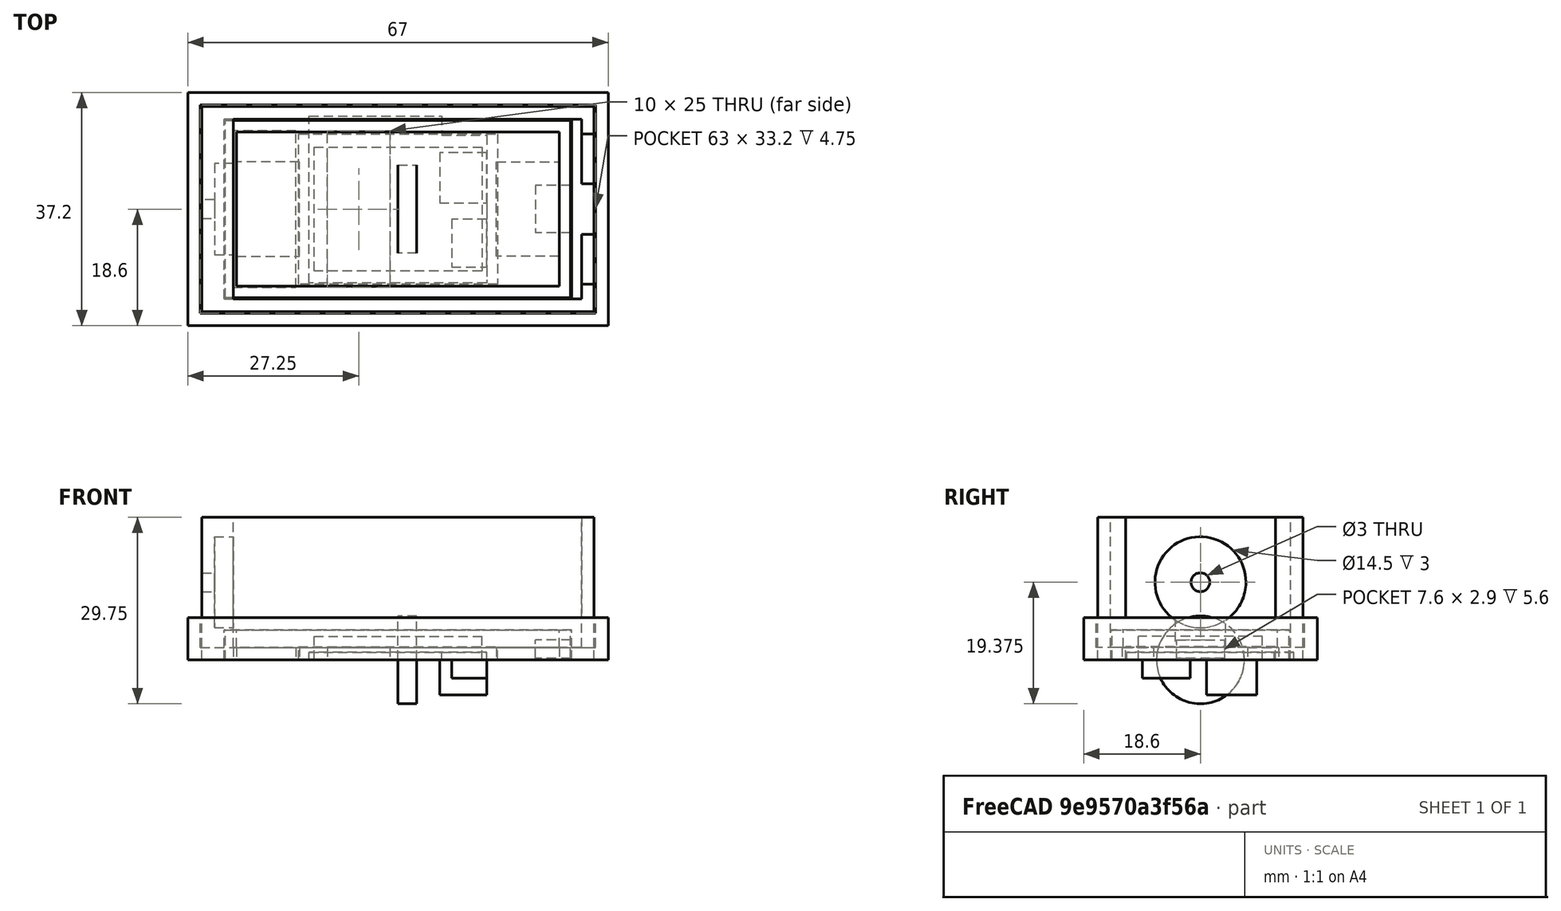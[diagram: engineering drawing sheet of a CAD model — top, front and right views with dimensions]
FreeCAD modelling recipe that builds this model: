
FCSTD DOCUMENT  (FreeCAD 0.20R29177 (Git))
Label: SniffingDetectorBox
License: All rights reserved
LicenseURL: http://en.wikipedia.org/wiki/All_rights_reserved
objects: Sketcher::SketchObject×20, PartDesign::Pad×13, PartDesign::Body×8, App::Part×8, PartDesign::Pocket×7, Mesh::Feature×2, Spreadsheet::Sheet×1
note: 68 computed .brp shape members not serialized (recipe doc carries the construction recipe); baked Part::Feature solids carry a one-line shape summary decoded from their .brp

FEATURE [Spreadsheet::Sheet] Spreadsheet  label="pars"
  cells = A1=ESPWidth; B1(ESPWidth)=28.2; A2=ESPLength; B2(ESPLength)=55; A3=USBWidth; B3(USBWidth)=7.6; A4=USBHeight; B4(USBHeight)=2.9; A5=USBLength; B5(USBLength)=5.6; A6=ESPHeight; B6(ESPHeight)=4.75; A7=ESPBoardHeight; B7(ESPBoardHeight)=1.6; A8=MicroDiam; B8(MicroDiam)=14; A9=MicroHeight; B9(MicroHeight)=3; A10=SDWidth; B10(SDWidth)=23.9; A11=SDLength; B11(SDLength)=31.7; A12=SDHeigth; B12(SDHeigth)=2.1; A13=ShieldWidthMax; B13(ShieldWidthMax)=26.6; A14=ShieldWidthMin; B14(ShieldWidthMin)=23.5; A15=ShieldLength; B15(ShieldLength)=28.3; A16=ShieldBoardHeight; B16(ShieldBoardHeight)=1.2; A17=ShieldPlugWidth; B17(ShieldPlugWidth)=8; A18=ShieldPlugHeight; B18(ShieldPlugHeight)=5.6; A19=ShieldPlugLength; B19(ShieldPlugLength)=7.5; A20=BatteryWidth; B20(BatteryWidth)=19.75; A21=BatteryLength; B21(BatteryLength)=26.75; A22=BatteryHeigth; B22(BatteryHeigth)=3.75; A23=Tolerance; B23(Tolerance)=0.5; A24=WallThick; B24(WallThick)=2
FEATURE [Sketcher::SketchObject] Sketch  label="BatterySketch"
  FullyConstrained = true
  MapMode = 5
  Support = -> [XY_Plane002]
  expr: Constraints[10] = <<pars>>.BatteryLength
  expr: Constraints[9] = <<pars>>.BatteryWidth
  sketch-geometry (4):
    g0: LineSegment StartX=-13.375 StartY=9.875 StartZ=0 EndX=13.375 EndY=9.875 EndZ=0
    g1: LineSegment StartX=13.375 StartY=9.875 StartZ=0 EndX=13.375 EndY=-9.875 EndZ=0
    g2: LineSegment StartX=13.375 StartY=-9.875 StartZ=0 EndX=-13.375 EndY=-9.875 EndZ=0
    g3: LineSegment StartX=-13.375 StartY=-9.875 StartZ=0 EndX=-13.375 EndY=9.875 EndZ=0
  constraints (11):
    c: Coincident(g0,g1)
    c: Coincident(g1,g2)
    c: Coincident(g2,g3)
    c: Coincident(g3,g0)
    c: Horizontal(g0)
    c: Horizontal(g2)
    c: Vertical(g1)
    c: Vertical(g3)
    c: Symmetric(g0,g1,g-1)
    c: DistanceY(g1,g1) = 19.75
    c: DistanceX(g0,g0) = 26.75
FEATURE [PartDesign::Pad] Pad
  Direction = (0,0,1)
  Length = 3.75
  Length2 = 10
  Profile = -> Sketch
  ReferenceAxis = -> Sketch [N_Axis]
  Type = 0
  expr: Length = <<pars>>.BatteryHeigth
FEATURE [PartDesign::Body] Body001  label="BatteryBody"
  Group = -> [Sketch,Pad]
  Origin = -> Origin002
  Tip = -> Pad
FEATURE [App::Part] Part001  label="Battery"
  Group = -> [Body001]
  Origin = -> Origin003
  Placement = pos=(-10,0,11.5) rot=(0,0,1;0rad)
FEATURE [Sketcher::SketchObject] Sketch001  label="SDCardSketch"
  FullyConstrained = true
  MapMode = 5
  Support = -> [XY_Plane005]
  expr: Constraints[10] = <<pars>>.SDLength
  expr: Constraints[9] = <<pars>>.SDWidth
  sketch-geometry (4):
    g0: LineSegment StartX=-15.85 StartY=11.95 StartZ=0 EndX=15.85 EndY=11.95 EndZ=0
    g1: LineSegment StartX=15.85 StartY=11.95 StartZ=0 EndX=15.85 EndY=-11.95 EndZ=0
    g2: LineSegment StartX=15.85 StartY=-11.95 StartZ=0 EndX=-15.85 EndY=-11.95 EndZ=0
    g3: LineSegment StartX=-15.85 StartY=-11.95 StartZ=0 EndX=-15.85 EndY=11.95 EndZ=0
  constraints (11):
    c: Coincident(g0,g1)
    c: Coincident(g1,g2)
    c: Coincident(g2,g3)
    c: Coincident(g3,g0)
    c: Horizontal(g0)
    c: Horizontal(g2)
    c: Vertical(g1)
    c: Vertical(g3)
    c: Symmetric(g0,g1,g-1)
    c: DistanceY(g1,g1) = 23.9
    c: DistanceX(g0,g0) = 31.7
FEATURE [PartDesign::Pad] Pad001
  Direction = (0,0,1)
  Length = 2.1
  Length2 = 10
  Profile = -> Sketch001
  ReferenceAxis = -> Sketch001 [N_Axis]
  Type = 0
  expr: Length = <<pars>>.SDHeigth
FEATURE [PartDesign::Body] Body002  label="SDCardBody"
  Group = -> [Sketch001,Pad001]
  Origin = -> Origin005
  Tip = -> Pad001
FEATURE [App::Part] Part002  label="SDCard"
  Group = -> [Body002]
  Origin = -> Origin004
  Placement = pos=(23,0,6.5) rot=(0,0,1;0rad)
FEATURE [Sketcher::SketchObject] Sketch002  label="MicroSketch"
  FullyConstrained = true
  MapMode = 5
  Placement = pos=(0,0,0) rot=(0.57735,0.57735,0.57735;2.0944rad)
  Support = -> [YZ_Plane007]
  expr: Constraints[1] = <<pars>>.MicroDiam
  sketch-geometry (1):
    g0: Circle CenterX=0 CenterY=0 CenterZ=0 NormalX=0 NormalY=0 NormalZ=1 AngleXU=0 Radius=7
  constraints (2):
    c: Coincident(g0,g-1)
    c: Diameter(g0) = 14
FEATURE [PartDesign::Pad] Pad002
  Direction = (1,-2e-16,3e-16)
  Length = 3
  Length2 = 10
  Placement = pos=(0,0,0) rot=(0.57735,0.57735,0.57735;2.0944rad)
  Profile = -> Sketch002
  ReferenceAxis = -> Sketch002 [N_Axis]
  Type = 0
  expr: Length = <<pars>>.MicroHeight
FEATURE [PartDesign::Body] Body003  label="MicroBody"
  Group = -> [Sketch002,Pad002]
  Origin = -> Origin007
  Tip = -> Pad002
FEATURE [App::Part] Part003  label="Micro"
  Group = -> [Body003]
  Origin = -> Origin006
  Placement = pos=(-29,0,12.5) rot=(0,0,1;0rad)
FEATURE [Sketcher::SketchObject] Sketch003  label="ESPSketch"
  FullyConstrained = true
  MapMode = 5
  Support = -> [XY_Plane009]
  expr: Constraints[10] = <<pars>>.ESPLength
  expr: Constraints[9] = <<pars>>.ESPWidth
  sketch-geometry (4):
    g0: LineSegment StartX=-27.5 StartY=14.1 StartZ=0 EndX=27.5 EndY=14.1 EndZ=0
    g1: LineSegment StartX=27.5 StartY=14.1 StartZ=0 EndX=27.5 EndY=-14.1 EndZ=0
    g2: LineSegment StartX=27.5 StartY=-14.1 StartZ=0 EndX=-27.5 EndY=-14.1 EndZ=0
    g3: LineSegment StartX=-27.5 StartY=-14.1 StartZ=0 EndX=-27.5 EndY=14.1 EndZ=0
  constraints (11):
    c: Coincident(g0,g1)
    c: Coincident(g1,g2)
    c: Coincident(g2,g3)
    c: Coincident(g3,g0)
    c: Horizontal(g0)
    c: Horizontal(g2)
    c: Vertical(g1)
    c: Vertical(g3)
    c: Symmetric(g0,g1,g-1)
    c: DistanceY(g1,g1) = 28.2
    c: DistanceX(g0,g0) = 55
FEATURE [PartDesign::Pad] Pad003
  Direction = (0,0,1)
  Length = 4.75
  Length2 = 10
  Profile = -> Sketch003
  ReferenceAxis = -> Sketch003 [N_Axis]
  Type = 0
  expr: Length = <<pars>>.ESPHeight
FEATURE [Sketcher::SketchObject] Sketch004
  ExternalGeometry = -> [Pad003]
  FullyConstrained = true
  MapMode = 5
  Placement = pos=(27.5,0,0) rot=(0.57735,0.57735,0.57735;2.0944rad)
  Support = -> [Pad003]
  expr: Constraints[10] = <<pars>>.ESPBoardHeight
  expr: Constraints[7] = Spreadsheet.USBHeight
  expr: Constraints[8] = Spreadsheet.USBWidth
  sketch-geometry (4):
    g0: LineSegment StartX=-3.8 StartY=3.15 StartZ=0 EndX=3.8 EndY=3.15 EndZ=0
    g1: LineSegment StartX=3.8 StartY=3.15 StartZ=0 EndX=3.8 EndY=0.25 EndZ=0
    g2: LineSegment StartX=3.8 StartY=0.25 StartZ=0 EndX=-3.8 EndY=0.25 EndZ=0
    g3: LineSegment StartX=-3.8 StartY=0.25 StartZ=0 EndX=-3.8 EndY=3.15 EndZ=0
  constraints (11):
    c: Coincident(g0,g1)
    c: Coincident(g1,g2)
    c: Coincident(g2,g3)
    c: Coincident(g3,g0)
    c: Horizontal(g0)
    c: Vertical(g1)
    c: Vertical(g3)
    c: DistanceY(g1,g1) = 2.9
    c: DistanceX(g0,g0) = 7.6
    c: Symmetric(g2,g1,g-2)
    c: DistanceY(g0,g-3) = 1.6
FEATURE [PartDesign::Pocket] Pocket
  BaseFeature = -> Pad003
  Direction = (-1,0,0)
  Length = 5.6
  Length2 = 5
  Profile = -> Sketch004
  ReferenceAxis = -> Sketch004 [N_Axis]
  Type = 0
  expr: Length = Spreadsheet.USBLength
FEATURE [PartDesign::Body] Body004  label="ESPBody"
  Group = -> [Sketch003,Pad003,Sketch004,Pocket]
  Origin = -> Origin009
  Tip = -> Pocket
FEATURE [App::Part] Part004  label="ESP"
  Group = -> [Body004]
  Origin = -> Origin008
  Placement = pos=(1.5,0,2) rot=(0,0,1;0rad)
FEATURE [Sketcher::SketchObject] Sketch005
  FullyConstrained = true
  MapMode = 5
  Support = -> [XY_Plane011]
  expr: Constraints[13] = <<pars>>.ShieldWidthMax - <<pars>>.ShieldWidthMin
  expr: Constraints[7] = <<pars>>.ShieldWidthMin
  expr: Constraints[8] = <<pars>>.ShieldLength
  sketch-geometry (6):
    g0: LineSegment StartX=7 StartY=11.75 StartZ=0 EndX=14.15 EndY=11.75 EndZ=0
    g1: LineSegment StartX=14.15 StartY=11.75 StartZ=0 EndX=14.15 EndY=-11.75 EndZ=0
    g2: LineSegment StartX=14.15 StartY=-11.75 StartZ=0 EndX=-14.15 EndY=-11.75 EndZ=0
    g3: LineSegment StartX=-14.15 StartY=-11.75 StartZ=0 EndX=-14.15 EndY=14.85 EndZ=0
    g4: LineSegment StartX=-14.15 StartY=14.85 StartZ=0 EndX=7 EndY=14.85 EndZ=0
    g5: LineSegment StartX=7 StartY=14.85 StartZ=0 EndX=7 EndY=11.75 EndZ=0
  constraints (17):
    c: Coincident(g0,g1)
    c: Coincident(g1,g2)
    c: Coincident(g2,g3)
    c: Horizontal(g0)
    c: Horizontal(g2)
    c: Vertical(g1)
    c: Vertical(g3)
    c: DistanceY(g1,g1) = 23.5
    c: DistanceX(g4,g0) = 28.3
    c: Coincident(g4,g5)
    c: Horizontal(g4)
    c: Vertical(g5)
    c: DistanceX(g4,g4) = 21.15
    c: DistanceY(g5,g5) = 3.1
    c: Coincident(g0,g5)
    c: Coincident(g3,g4)
    c: Symmetric(g0,g2,g-1)
FEATURE [PartDesign::Pad] Pad004
  Direction = (0,0,1)
  Length = 1.2
  Length2 = 10
  Profile = -> Sketch005
  ReferenceAxis = -> Sketch005 [N_Axis]
  Type = 0
  expr: Length = <<pars>>.ShieldBoardHeight
FEATURE [Sketcher::SketchObject] Sketch006
  ExternalGeometry = -> [Pad004]
  FullyConstrained = true
  MapMode = 5
  Placement = pos=(0,0,0) rot=(1,0,0;3.14159rad)
  Support = -> [Pad004]
  expr: Constraints[8] = <<pars>>.ShieldPlugWidth
  expr: Constraints[9] = <<pars>>.ShieldPlugLength
  sketch-geometry (4):
    g0: LineSegment StartX=6.65 StartY=-1 StartZ=0 EndX=14.15 EndY=-1 EndZ=0
    g1: LineSegment StartX=14.15 StartY=-1 StartZ=0 EndX=14.15 EndY=-9 EndZ=0
    g2: LineSegment StartX=14.15 StartY=-9 StartZ=0 EndX=6.65 EndY=-9 EndZ=0
    g3: LineSegment StartX=6.65 StartY=-9 StartZ=0 EndX=6.65 EndY=-1 EndZ=0
  constraints (12):
    c: Coincident(g0,g1)
    c: Coincident(g1,g2)
    c: Coincident(g2,g3)
    c: Coincident(g3,g0)
    c: Horizontal(g0)
    c: Horizontal(g2)
    c: Vertical(g1)
    c: Vertical(g3)
    c: DistanceY(g1,g1) = 8
    c: DistanceX(g2,g2) = 7.5
    c: PointOnObject(g1,g-3)
    c: DistanceY(g-3,g1) = 2.75
FEATURE [PartDesign::Pad] Pad005
  BaseFeature = -> Pad004
  Direction = (0,0,-1)
  Length = 5.6
  Length2 = 10
  Profile = -> Sketch006
  ReferenceAxis = -> Sketch006 [N_Axis]
  Type = 0
  expr: Length = <<pars>>.ShieldPlugHeight
FEATURE [Sketcher::SketchObject] Sketch007
  ExternalGeometry = -> [Pad005]
  FullyConstrained = true
  MapMode = 5
  Placement = pos=(0,0,0) rot=(1,0,0;3.14159rad)
  Support = -> [Pad005]
  expr: Constraints[8] = <<pars>>.USBWidth
  expr: Constraints[9] = <<pars>>.USBLength
  sketch-geometry (4):
    g0: LineSegment StartX=8.55 StartY=9.25 StartZ=0 EndX=14.15 EndY=9.25 EndZ=0
    g1: LineSegment StartX=14.15 StartY=9.25 StartZ=0 EndX=14.15 EndY=1.65 EndZ=0
    g2: LineSegment StartX=14.15 StartY=1.65 StartZ=0 EndX=8.55 EndY=1.65 EndZ=0
    g3: LineSegment StartX=8.55 StartY=1.65 StartZ=0 EndX=8.55 EndY=9.25 EndZ=0
  constraints (12):
    c: Coincident(g0,g1)
    c: Coincident(g1,g2)
    c: Coincident(g2,g3)
    c: Coincident(g3,g0)
    c: Horizontal(g0)
    c: Horizontal(g2)
    c: Vertical(g1)
    c: Vertical(g3)
    c: DistanceY(g1,g1) = 7.6
    c: DistanceX(g0,g0) = 5.6
    c: PointOnObject(g1,g-3)
    c: DistanceY(g0,g-3) = 2.5
FEATURE [PartDesign::Pad] Pad006
  BaseFeature = -> Pad005
  Direction = (0,0,-1)
  Length = 2.9
  Length2 = 10
  Profile = -> Sketch007
  ReferenceAxis = -> Sketch007 [N_Axis]
  Type = 0
  expr: Length = <<pars>>.USBHeight
FEATURE [PartDesign::Body] Body005  label="ShieldBody"
  Group = -> [Sketch005,Pad004,Sketch006,Pad005,Sketch007,Pad006]
  Origin = -> Origin011
  Tip = -> Pad006
FEATURE [App::Part] Part005  label="Shield"
  Group = -> [Body005]
  Origin = -> Origin010
  Placement = pos=(22,0,14.5) rot=(0,0,1;0rad)
FEATURE [Sketcher::SketchObject] Sketch008
  FullyConstrained = true
  MapMode = 5
  Support = -> [XY_Plane]
  expr: Constraints[10] = <<pars>>.ESPLength + <<pars>>.Tolerance + 2 * <<pars>>.WallThick + <<pars>>.MicroHeight
  expr: Constraints[9] = <<pars>>.ESPWidth + <<pars>>.Tolerance + 2 * <<pars>>.WallThick
  sketch-geometry (4):
    g0: LineSegment StartX=-31.25 StartY=16.35 StartZ=0 EndX=31.25 EndY=16.35 EndZ=0
    g1: LineSegment StartX=31.25 StartY=16.35 StartZ=0 EndX=31.25 EndY=-16.35 EndZ=0
    g2: LineSegment StartX=31.25 StartY=-16.35 StartZ=0 EndX=-31.25 EndY=-16.35 EndZ=0
    g3: LineSegment StartX=-31.25 StartY=-16.35 StartZ=0 EndX=-31.25 EndY=16.35 EndZ=0
  constraints (11):
    c: Coincident(g0,g1)
    c: Coincident(g1,g2)
    c: Coincident(g2,g3)
    c: Coincident(g3,g0)
    c: Horizontal(g0)
    c: Horizontal(g2)
    c: Vertical(g1)
    c: Vertical(g3)
    c: Symmetric(g0,g1,g-1)
    c: DistanceY(g1,g1) = 32.7
    c: DistanceX(g2,g2) = 62.5
FEATURE [PartDesign::Pad] Pad007
  Direction = (0,0,1)
  Length = 2
  Length2 = 10
  Profile = -> Sketch008
  ReferenceAxis = -> Sketch008 [N_Axis]
  Type = 0
  expr: Length = <<pars>>.WallThick
FEATURE [Sketcher::SketchObject] Sketch009
  ExternalGeometry = -> [Pad007]
  FullyConstrained = true
  MapMode = 5
  Placement = pos=(0,0,2) rot=(0,0,1;0rad)
  Support = -> [Pad007]
  expr: Constraints[16] = <<pars>>.WallThick
  expr: Constraints[17] = <<pars>>.WallThick
  expr: Constraints[27] = <<pars>>.WallThick
  expr: Constraints[6] = <<pars>>.WallThick + <<pars>>.MicroHeight
  sketch-geometry (12):
    g0: LineSegment StartX=-31.25 StartY=16.35 StartZ=0 EndX=-26.25 EndY=16.35 EndZ=0
    g1: LineSegment StartX=-26.25 StartY=14.35 StartZ=0 EndX=-26.25 EndY=-14.35 EndZ=0
    g2: LineSegment StartX=-26.25 StartY=-16.35 StartZ=0 EndX=-31.25 EndY=-16.35 EndZ=0
    g3: LineSegment StartX=-31.25 StartY=-16.35 StartZ=0 EndX=-31.25 EndY=16.35 EndZ=0
    g4: LineSegment StartX=-26.25 StartY=16.35 StartZ=0 EndX=31.25 EndY=16.35 EndZ=0
    g5: LineSegment StartX=31.25 StartY=16.35 StartZ=0 EndX=31.25 EndY=14.35 EndZ=0
    g6: LineSegment StartX=29.25 StartY=14.35 StartZ=0 EndX=-26.25 EndY=14.35 EndZ=0
    g7: LineSegment StartX=-26.25 StartY=-16.35 StartZ=0 EndX=31.25 EndY=-16.35 EndZ=0
    g8: LineSegment StartX=31.25 StartY=-16.35 StartZ=0 EndX=31.25 EndY=-14.35 EndZ=0
    g9: LineSegment StartX=29.25 StartY=-14.35 StartZ=0 EndX=-26.25 EndY=-14.35 EndZ=0
    g10: LineSegment StartX=31.25 StartY=14.35 StartZ=0 EndX=31.25 EndY=-14.35 EndZ=0
    g11: LineSegment StartX=29.25 StartY=14.35 StartZ=0 EndX=29.25 EndY=-14.35 EndZ=0
  constraints (32):
    c: Coincident(g2,g3)
    c: Coincident(g3,g0)
    c: Horizontal(g0)
    c: Horizontal(g2)
    c: Vertical(g1)
    c: Coincident(g0,g-3)
    c: Coincident(g2,g-3) = 5
    c: DistanceX(g0,g0) = 5
    c: Coincident(g4,g5)
    c: Horizontal(g6)
    c: Vertical(g5)
    c: Coincident(g4,g0)
    c: Coincident(g7,g8)
    c: Horizontal(g9)
    c: Vertical(g8)
    c: Coincident(g-4,g4)
    c: Coincident(g-5,g7) = 2
    c: DistanceY(g5,g5) = 2
    c: DistanceY(g8,g8) = 2
    c: Coincident(g1,g6)
    c: Coincident(g9,g1)
    c: Vertical(g1,g0)
    c: Vertical(g2,g1)
    c: Coincident(g7,g2)
    c: Coincident(g10,g5)
    c: Coincident(g10,g8)
    c: Vertical(g11)
    c: DistanceX(g11,g5) = 2
    c: Coincident(g6,g11)
    c: Horizontal(g5,g6)
    c: Coincident(g9,g11)
    c: Horizontal(g8,g9)
FEATURE [PartDesign::Pad] Pad008
  BaseFeature = -> Pad007
  Direction = (0,0,1)
  Length = 20.75
  Length2 = 10
  Profile = -> Sketch009
  ReferenceAxis = -> Sketch009 [N_Axis]
  Type = 0
  expr: Length = <<pars>>.ESPHeight + <<pars>>.MicroDiam + <<pars>>.WallThick
FEATURE [Sketcher::SketchObject] Sketch010
  ExternalGeometry = -> [Pad008]
  FullyConstrained = true
  MapMode = 5
  Placement = pos=(-26.25,0,0) rot=(0.57735,0.57735,0.57735;2.0944rad)
  Support = -> [Pad008]
  expr: Constraints[0] = <<pars>>.MicroDiam + <<pars>>.Tolerance
  sketch-geometry (1):
    g0: Circle CenterX=0 CenterY=12.375 CenterZ=0 NormalX=0 NormalY=0 NormalZ=1 AngleXU=0 Radius=7.25
  constraints (2):
    c: Diameter(g0) = 14.5
    c: Symmetric(g-3,g-4,g0)
FEATURE [PartDesign::Pocket] Pocket001
  BaseFeature = -> Pad008
  Direction = (-1,0,0)
  Length = 3
  Length2 = 5
  Profile = -> Sketch010
  ReferenceAxis = -> Sketch010 [N_Axis]
  Type = 0
  expr: Length = <<pars>>.MicroHeight
FEATURE [Sketcher::SketchObject] Sketch011
  ExternalGeometry = -> [Pocket001]
  FullyConstrained = true
  MapMode = 5
  Placement = pos=(-29.25,0,0) rot=(0.57735,0.57735,0.57735;2.0944rad)
  Support = -> [Pocket001]
  sketch-geometry (1):
    g0: Circle CenterX=0 CenterY=12.375 CenterZ=0 NormalX=0 NormalY=0 NormalZ=1 AngleXU=0 Radius=1.5
  constraints (2):
    c: Coincident(g0,g-3)
    c: Diameter(g0) = 3
FEATURE [PartDesign::Pocket] Pocket002
  BaseFeature = -> Pocket001
  Direction = (-1,0,0)
  Length = 2
  Length2 = 5
  Profile = -> Sketch011
  ReferenceAxis = -> Sketch011 [N_Axis]
  Type = 0
  expr: Length = <<pars>>.WallThick
FEATURE [Sketcher::SketchObject] Sketch012
  ExternalGeometry = -> [Pocket002]
  FullyConstrained = true
  MapMode = 5
  Placement = pos=(31.25,0,0) rot=(0.57735,0.57735,0.57735;2.0944rad)
  Support = -> [Pocket002]
  expr: Constraints[7] = <<pars>>.SDWidth
  expr: Constraints[8] = <<pars>>.ESPHeight
  sketch-geometry (4):
    g0: LineSegment StartX=-11.95 StartY=22.75 StartZ=0 EndX=11.95 EndY=22.75 EndZ=0
    g1: LineSegment StartX=11.95 StartY=22.75 StartZ=0 EndX=11.95 EndY=6.75 EndZ=0
    g2: LineSegment StartX=11.95 StartY=6.75 StartZ=0 EndX=-11.95 EndY=6.75 EndZ=0
    g3: LineSegment StartX=-11.95 StartY=6.75 StartZ=0 EndX=-11.95 EndY=22.75 EndZ=0
  constraints (11):
    c: Coincident(g0,g1)
    c: Coincident(g1,g2)
    c: Coincident(g2,g3)
    c: Coincident(g3,g0)
    c: Horizontal(g0)
    c: Vertical(g1)
    c: Vertical(g3)
    c: DistanceX(g2,g2) = 23.9
    c: DistanceY(g-4,g2) = 4.75
    c: Symmetric(g1,g2,g-2)
    c: PointOnObject(g0,g-3)
FEATURE [PartDesign::Pocket] Pocket003
  BaseFeature = -> Pocket002
  Direction = (-1,0,0)
  Length = 2
  Length2 = 5
  Profile = -> Sketch012
  ReferenceAxis = -> Sketch012 [N_Axis]
  Type = 0
  expr: Length = <<pars>>.WallThick
FEATURE [Sketcher::SketchObject] Sketch013
  FullyConstrained = true
  MapMode = 5
  Support = -> [XY_Plane013]
  expr: Constraints[10] = <<pars>>.ESPLength + <<pars>>.Tolerance + 2 * <<pars>>.WallThick + <<pars>>.MicroHeight + <<pars>>.Tolerance + 2 * <<pars>>.WallThick
  expr: Constraints[8] = <<pars>>.ESPWidth + 2 * <<pars>>.WallThick + 2 * <<pars>>.Tolerance + 2 * <<pars>>.WallThick
  sketch-geometry (4):
    g0: LineSegment StartX=-33.5 StartY=18.6 StartZ=0 EndX=33.5 EndY=18.6 EndZ=0
    g1: LineSegment StartX=33.5 StartY=18.6 StartZ=0 EndX=33.5 EndY=-18.6 EndZ=0
    g2: LineSegment StartX=33.5 StartY=-18.6 StartZ=0 EndX=-33.5 EndY=-18.6 EndZ=0
    g3: LineSegment StartX=-33.5 StartY=-18.6 StartZ=0 EndX=-33.5 EndY=18.6 EndZ=0
  constraints (11):
    c: Coincident(g0,g1)
    c: Coincident(g1,g2)
    c: Coincident(g2,g3)
    c: Coincident(g3,g0)
    c: Horizontal(g0)
    c: Horizontal(g2)
    c: Vertical(g1)
    c: Vertical(g3)
    c: DistanceY(g3,g3) = 37.2
    c: Symmetric(g2,g0,g-1)
    c: DistanceX(g2,g2) = 67
FEATURE [PartDesign::Pad] Pad009
  Direction = (0,0,1)
  Length = 2
  Length2 = 10
  Profile = -> Sketch013
  ReferenceAxis = -> Sketch013 [N_Axis]
  Type = 0
  expr: Length = <<pars>>.WallThick
FEATURE [Sketcher::SketchObject] Sketch014
  ExternalGeometry = -> [Pad009]
  FullyConstrained = true
  MapMode = 5
  Placement = pos=(0,0,2) rot=(0,0,1;0rad)
  Support = -> [Pad009]
  expr: Constraints[19] = <<pars>>.WallThick
  expr: Constraints[20] = <<pars>>.WallThick
  sketch-geometry (8):
    g0: LineSegment StartX=-33.5 StartY=18.6 StartZ=0 EndX=33.5 EndY=18.6 EndZ=0
    g1: LineSegment StartX=33.5 StartY=18.6 StartZ=0 EndX=33.5 EndY=-18.6 EndZ=0
    g2: LineSegment StartX=33.5 StartY=-18.6 StartZ=0 EndX=-33.5 EndY=-18.6 EndZ=0
    g3: LineSegment StartX=-33.5 StartY=-18.6 StartZ=0 EndX=-33.5 EndY=18.6 EndZ=0
    g4: LineSegment StartX=-31.5 StartY=16.6 StartZ=0 EndX=31.5 EndY=16.6 EndZ=0
    g5: LineSegment StartX=31.5 StartY=16.6 StartZ=0 EndX=31.5 EndY=-16.6 EndZ=0
    g6: LineSegment StartX=31.5 StartY=-16.6 StartZ=0 EndX=-31.5 EndY=-16.6 EndZ=0
    g7: LineSegment StartX=-31.5 StartY=-16.6 StartZ=0 EndX=-31.5 EndY=16.6 EndZ=0
  constraints (21):
    c: Coincident(g0,g1)
    c: Coincident(g1,g2)
    c: Coincident(g2,g3)
    c: Coincident(g3,g0)
    c: Horizontal(g0)
    c: Horizontal(g2)
    c: Vertical(g1)
    c: Vertical(g3)
    c: Coincident(g0,g-3)
    c: Coincident(g1,g-4)
    c: Coincident(g4,g5)
    c: Coincident(g5,g6)
    c: Coincident(g6,g7)
    c: Coincident(g7,g4)
    c: Horizontal(g4)
    c: Horizontal(g6)
    c: Vertical(g5)
    c: Vertical(g7)
    c: Symmetric(g4,g6,g-1)
    c: DistanceX(g0,g4) = 2
    c: DistanceY(g4,g0) = 2
FEATURE [PartDesign::Pad] Pad010
  BaseFeature = -> Pad009
  Direction = (0,0,1)
  Length = 4.75
  Length2 = 10
  Profile = -> Sketch014
  ReferenceAxis = -> Sketch014 [N_Axis]
  Type = 0
  expr: Length = <<pars>>.ESPHeight
FEATURE [PartDesign::Body] Body006  label="LidBody"
  Group = -> [Sketch013,Pad009,Sketch014,Pad010]
  Origin = -> Origin013
  Tip = -> Pad010
FEATURE [App::Part] Part006  label="Lid"
  Group = -> [Body006]
  Origin = -> Origin012
  Placement = pos=(0,3.6e-15,29) rot=(1,0,0;3.14159rad)
FEATURE [Sketcher::SketchObject] Sketch015
  FullyConstrained = true
  MapMode = 5
  Support = -> [XY_Plane015]
  expr: Constraints[10] = <<pars>>.ESPWidth + <<pars>>.Tolerance - 0.1
  expr: Constraints[9] = <<pars>>.ESPLength + <<pars>>.Tolerance - 0.1
  sketch-geometry (4):
    g0: LineSegment StartX=-27.7 StartY=14.3 StartZ=0 EndX=27.7 EndY=14.3 EndZ=0
    g1: LineSegment StartX=27.7 StartY=14.3 StartZ=0 EndX=27.7 EndY=-14.3 EndZ=0
    g2: LineSegment StartX=27.7 StartY=-14.3 StartZ=0 EndX=-27.7 EndY=-14.3 EndZ=0
    g3: LineSegment StartX=-27.7 StartY=-14.3 StartZ=0 EndX=-27.7 EndY=14.3 EndZ=0
  constraints (11):
    c: Coincident(g0,g1)
    c: Coincident(g1,g2)
    c: Coincident(g2,g3)
    c: Coincident(g3,g0)
    c: Horizontal(g0)
    c: Horizontal(g2)
    c: Vertical(g1)
    c: Vertical(g3)
    c: Symmetric(g0,g1,g-1)
    c: DistanceX(g0,g0) = 55.4
    c: DistanceY(g1,g1) = 28.6
FEATURE [PartDesign::Pad] Pad011
  Direction = (0,0,1)
  Length = 2
  Length2 = 10
  Profile = -> Sketch015
  ReferenceAxis = -> Sketch015 [N_Axis]
  Type = 0
  expr: Length = <<pars>>.WallThick
FEATURE [Sketcher::SketchObject] Sketch016
  ExternalGeometry = -> [Pad011]
  FullyConstrained = true
  MapMode = 5
  Placement = pos=(0,0,2) rot=(0,0,1;0rad)
  Support = -> [Pad011]
  expr: Constraints[10] = <<pars>>.WallThick
  expr: Constraints[9] = <<pars>>.WallThick
  sketch-geometry (8):
    g0: LineSegment StartX=-25.7 StartY=12.3 StartZ=0 EndX=25.7 EndY=12.3 EndZ=0
    g1: LineSegment StartX=25.7 StartY=12.3 StartZ=0 EndX=25.7 EndY=-12.3 EndZ=0
    g2: LineSegment StartX=25.7 StartY=-12.3 StartZ=0 EndX=-25.7 EndY=-12.3 EndZ=0
    g3: LineSegment StartX=-25.7 StartY=-12.3 StartZ=0 EndX=-25.7 EndY=12.3 EndZ=0
    g4: LineSegment StartX=27.7 StartY=14.3 StartZ=0 EndX=-27.7 EndY=14.3 EndZ=0
    g5: LineSegment StartX=-27.7 StartY=14.3 StartZ=0 EndX=-27.7 EndY=-14.3 EndZ=0
    g6: LineSegment StartX=-27.7 StartY=-14.3 StartZ=0 EndX=27.7 EndY=-14.3 EndZ=0
    g7: LineSegment StartX=27.7 StartY=-14.3 StartZ=0 EndX=27.7 EndY=14.3 EndZ=0
  constraints (21):
    c: Coincident(g0,g1)
    c: Coincident(g1,g2)
    c: Coincident(g2,g3)
    c: Coincident(g3,g0)
    c: Horizontal(g0)
    c: Horizontal(g2)
    c: Vertical(g1)
    c: Vertical(g3)
    c: Symmetric(g0,g2,g-1)
    c: DistanceY(g0,g-3) = 2
    c: DistanceX(g-3,g0) = 2
    c: Coincident(g4,g5)
    c: Coincident(g5,g6)
    c: Coincident(g6,g7)
    c: Coincident(g7,g4)
    c: Horizontal(g4)
    c: Horizontal(g6)
    c: Vertical(g5)
    c: Vertical(g7)
    c: Coincident(g4,g-3)
    c: Coincident(g5,g-4)
FEATURE [PartDesign::Pad] Pad012
  BaseFeature = -> Pad011
  Direction = (0,0,1)
  Length = 2.75
  Length2 = 10
  Profile = -> Sketch016
  ReferenceAxis = -> Sketch016 [N_Axis]
  Type = 0
  expr: Length = <<pars>>.ESPHeight - <<pars>>.WallThick
FEATURE [Sketcher::SketchObject] Sketch017
  ExternalGeometry = -> [Pocket003]
  FullyConstrained = true
  MapMode = 5
  Placement = pos=(0,0,0) rot=(0.57735,0.57735,0.57735;2.0944rad)
  Support = -> [YZ_Plane]
  expr: Constraints[8] = <<pars>>.USBWidth + <<pars>>.Tolerance
  expr: Constraints[9] = <<pars>>.ESPHeight
  sketch-geometry (4):
    g0: LineSegment StartX=-4.05 StartY=6.75 StartZ=0 EndX=4.05 EndY=6.75 EndZ=0
    g1: LineSegment StartX=4.05 StartY=6.75 StartZ=0 EndX=4.05 EndY=2 EndZ=0
    g2: LineSegment StartX=4.05 StartY=2 StartZ=0 EndX=-4.05 EndY=2 EndZ=0
    g3: LineSegment StartX=-4.05 StartY=2 StartZ=0 EndX=-4.05 EndY=6.75 EndZ=0
  constraints (11):
    c: Coincident(g0,g1)
    c: Coincident(g1,g2)
    c: Coincident(g2,g3)
    c: Coincident(g3,g0)
    c: Horizontal(g2)
    c: Vertical(g1)
    c: Vertical(g3)
    c: Symmetric(g0,g0,g-2)
    c: DistanceX(g2,g2) = 8.1
    c: DistanceY(g1,g1) = 4.75
    c: PointOnObject(g0,g-4)
FEATURE [PartDesign::Pocket] Pocket004
  BaseFeature = -> Pocket003
  Direction = (-1,2e-16,-3e-16)
  Length = 40
  Length2 = 5
  Profile = -> Sketch017
  ReferenceAxis = -> Sketch017 [N_Axis]
  Reversed = true
  Type = 0
  expr: Length = 40
FEATURE [Sketcher::SketchObject] Sketch018
  ExternalGeometry = -> [Pad008]
  FullyConstrained = true
  MapMode = 5
  Placement = pos=(0,0,2) rot=(0,0,1;0rad)
  Support = -> [Pad008]
  sketch-geometry (8):
    g0: LineSegment StartX=-26.25 StartY=12.5 StartZ=0 EndX=-16.25 EndY=12.5 EndZ=0
    g1: LineSegment StartX=-16.25 StartY=12.5 StartZ=0 EndX=-16.25 EndY=-12.5 EndZ=0
    g2: LineSegment StartX=-16.25 StartY=-12.5 StartZ=0 EndX=-26.25 EndY=-12.5 EndZ=0
    g3: LineSegment StartX=-26.25 StartY=-12.5 StartZ=0 EndX=-26.25 EndY=12.5 EndZ=0
    g4: LineSegment StartX=-11.25 StartY=12.5 StartZ=0 EndX=-1.25 EndY=12.5 EndZ=0
    g5: LineSegment StartX=-1.25 StartY=12.5 StartZ=0 EndX=-1.25 EndY=-12.5 EndZ=0
    g6: LineSegment StartX=-1.25 StartY=-12.5 StartZ=0 EndX=-11.25 EndY=-12.5 EndZ=0
    g7: LineSegment StartX=-11.25 StartY=-12.5 StartZ=0 EndX=-11.25 EndY=12.5 EndZ=0
  constraints (23):
    c: Coincident(g0,g1)
    c: Coincident(g1,g2)
    c: Coincident(g2,g3)
    c: Coincident(g3,g0)
    c: Horizontal(g0)
    c: Horizontal(g2)
    c: Vertical(g1)
    c: Symmetric(g0,g2,g-1)
    c: DistanceY(g3,g3) = 25
    c: PointOnObject(g0,g-3)
    c: DistanceX(g0,g0) = 10
    c: Coincident(g4,g5)
    c: Coincident(g5,g6)
    c: Coincident(g6,g7)
    c: Coincident(g7,g4)
    c: Horizontal(g4)
    c: Horizontal(g6)
    c: Vertical(g5)
    c: Vertical(g7)
    c: Horizontal(g4,g0)
    c: Horizontal(g6,g1)
    c: DistanceX(g4,g4) = 10
    c: DistanceX(g0,g4) = 5
FEATURE [PartDesign::Pocket] Pocket005
  BaseFeature = -> Pocket004
  Direction = (0,0,-1)
  Length = 5
  Length2 = 5
  Profile = -> Sketch018
  ReferenceAxis = -> Sketch018 [N_Axis]
  Type = 2
FEATURE [PartDesign::Body] Body  label="BoxBody"
  Group = -> [Sketch008,Pad007,Sketch009,Pad008,Sketch010,Pocket001,Sketch011,Pocket002,Sketch012,Pocket003,Sketch017,Pocket004,Sketch018,Pocket005]
  Origin = -> Origin
  Tip = -> Pocket005
FEATURE [App::Part] Part  label="Box"
  Group = -> [Body]
  Origin = -> Origin001
FEATURE [Sketcher::SketchObject] Sketch019
  ExternalGeometry = -> [Pad012]
  FullyConstrained = true
  MapMode = 5
  Placement = pos=(0,0,2) rot=(0,0,1;0rad)
  Support = -> [Pad012]
  sketch-geometry (8):
    g0: LineSegment StartX=-25.7 StartY=7.5 StartZ=0 EndX=-15.7 EndY=7.5 EndZ=0
    g1: LineSegment StartX=-15.7 StartY=7.5 StartZ=0 EndX=-15.7 EndY=-7.5 EndZ=0
    g2: LineSegment StartX=-15.7 StartY=-7.5 StartZ=0 EndX=-25.7 EndY=-7.5 EndZ=0
    g3: LineSegment StartX=-25.7 StartY=-7.5 StartZ=0 EndX=-25.7 EndY=7.5 EndZ=0
    g4: LineSegment StartX=15.7 StartY=7.5 StartZ=0 EndX=25.7 EndY=7.5 EndZ=0
    g5: LineSegment StartX=25.7 StartY=7.5 StartZ=0 EndX=25.7 EndY=-7.5 EndZ=0
    g6: LineSegment StartX=25.7 StartY=-7.5 StartZ=0 EndX=15.7 EndY=-7.5 EndZ=0
    g7: LineSegment StartX=15.7 StartY=-7.5 StartZ=0 EndX=15.7 EndY=7.5 EndZ=0
  constraints (23):
    c: Coincident(g0,g1)
    c: Coincident(g1,g2)
    c: Coincident(g2,g3)
    c: Coincident(g3,g0)
    c: Horizontal(g0)
    c: Horizontal(g2)
    c: Vertical(g1)
    c: Symmetric(g0,g2,g-1)
    c: DistanceY(g3,g3) = 15
    c: DistanceX(g0,g0) = 10
    c: PointOnObject(g0,g-3)
    c: Coincident(g4,g5)
    c: Coincident(g5,g6)
    c: Coincident(g6,g7)
    c: Coincident(g7,g4)
    c: Horizontal(g4)
    c: Horizontal(g6)
    c: Vertical(g5)
    c: Vertical(g7)
    c: Horizontal(g4,g0)
    c: Horizontal(g6,g1)
    c: PointOnObject(g4,g-4)
    c: DistanceX(g4,g4) = 10
FEATURE [PartDesign::Pocket] Pocket006
  BaseFeature = -> Pad012
  Direction = (0,0,-1)
  Length = 5
  Length2 = 5
  Profile = -> Sketch019
  ReferenceAxis = -> Sketch019 [N_Axis]
  Type = 2
FEATURE [PartDesign::Body] Body007  label="LidInternBody"
  Group = -> [Sketch015,Pad011,Sketch016,Pad012,Sketch019,Pocket006]
  Origin = -> Origin015
  Tip = -> Pocket006
FEATURE [App::Part] Part007  label="LidIntern"
  Group = -> [Body007]
  Origin = -> Origin014
  Placement = pos=(1.5,0,23) rot=(0,-1,0;3.14159rad)
FEATURE [Mesh::Feature] Mesh  label="LidInternBody (Meshed)"
FEATURE [Mesh::Feature] Mesh001  label="BoxBody (Meshed)"
